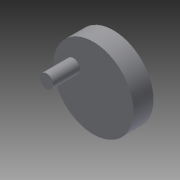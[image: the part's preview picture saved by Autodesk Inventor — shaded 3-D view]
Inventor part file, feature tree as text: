
AUTODESK INVENTOR PART (.ipt)
format: ipt  version: 2014 (Build 180170000, 170)  size: 81,408 bytes
history: native  units: in
note: dims shown in document units (in); Inventor stores cm internally (conversion verified against a paired STEP export)
features: extrude x2, sketch x2
ambient origin geometry x8: Origin, YZ Plane, XZ Plane, XY Plane, X Axis, Y Axis, Z Axis, Center Point
bodies: Solid1 (feature_tree)
feature tree (4):
  extrude  "Extrusion1"  Depth=0.75in TaperAngle=0.0deg
  extrude  "Extrusion2"  Depth=0.75in
  sketch  "Sketch1"  dims[d0=3.0in d1=0.75in d2=0.0in]
  sketch  "Sketch2"  dims[d3=0.5in d4=0.75in d5=0.35in d6=1.0in d7=0.0in]
